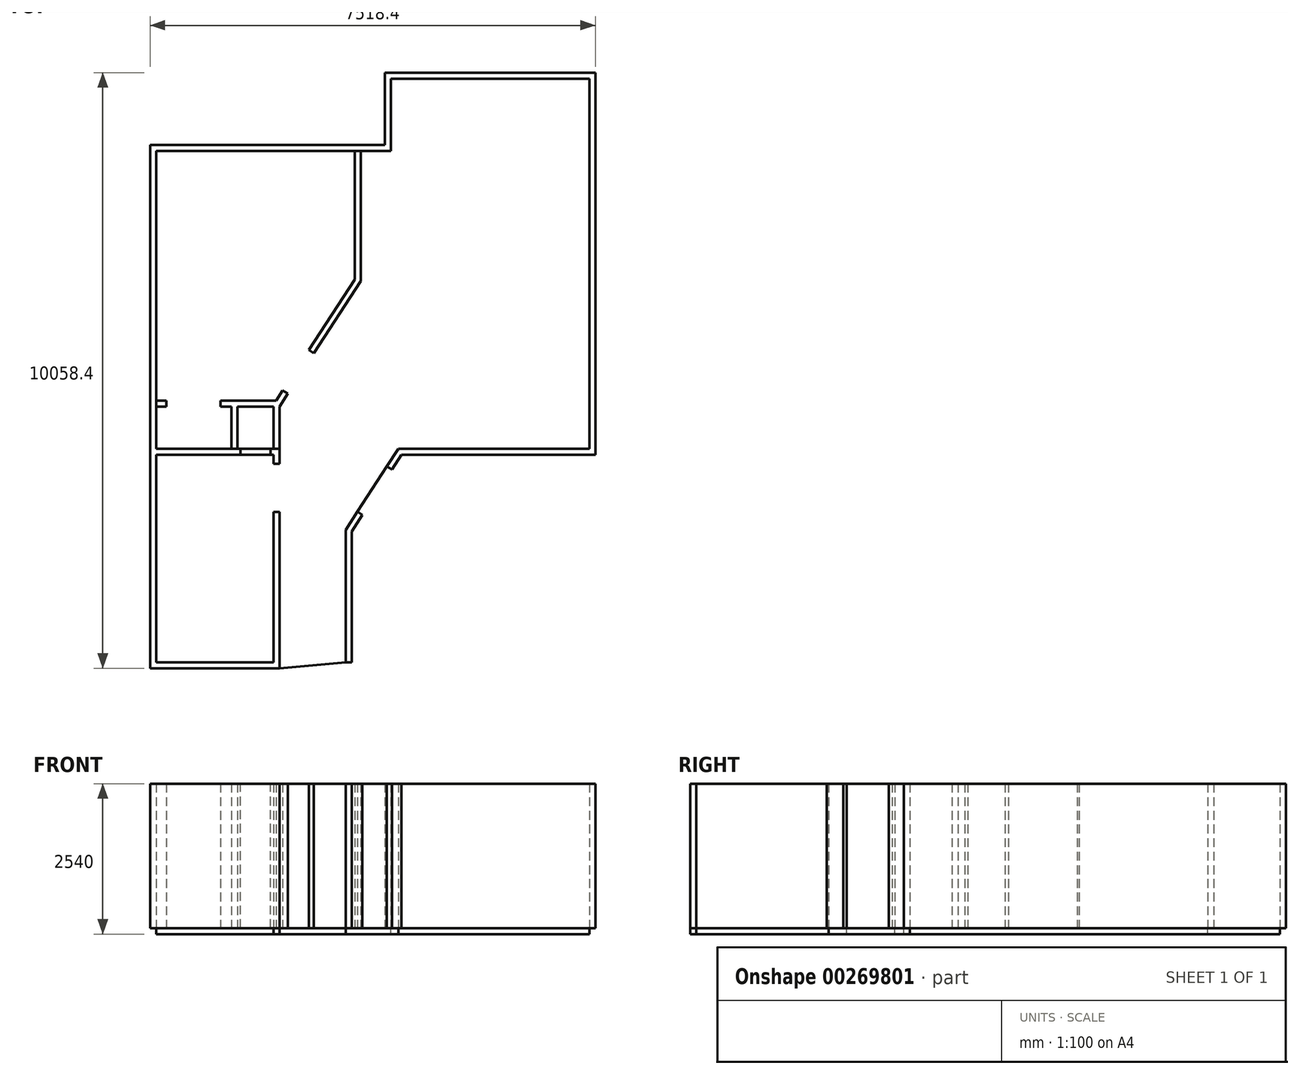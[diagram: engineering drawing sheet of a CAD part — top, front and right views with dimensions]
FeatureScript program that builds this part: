
annotation { "Feature Type Name" : "Feature", "Feature Type Description" : "" }
export const myFeature = defineFeature(function(context is Context, id is Id, definition is map)
    precondition{}
    {
        {
            var Q0;
            Q0=qCreatedBy(makeId("Top.planeOp"),FACE);
            var sketch = newSketch(context, id + "F0", { "sketchPlane" : qUnion([Q0])});
            skLineSegment(sketch, "E0", {"start": v(-1219.2, -1524) * mm, "end": v(-1219.2, -3606.8) * mm});
            skLineSegment(sketch, "E1", {"start": v(-1219.2, -3606.8) * mm, "end": v(-3200.4, -3606.8) * mm});
            skLineSegment(sketch, "E2", {"start": v(-3200.4, -3606.8) * mm, "end": v(-3200.4, -101.6) * mm});
            skLineSegment(sketch, "E3", {"start": v(-3200.4, 5029.2) * mm, "end": v(762, 5029.2) * mm});
            skLineSegment(sketch, "E4", {"start": v(762, 5029.2) * mm, "end": v(762, 6248.4) * mm});
            skLineSegment(sketch, "E5", {"start": v(762, 6248.4) * mm, "end": v(4114.8, 6248.4) * mm});
            skLineSegment(sketch, "E6", {"start": v(4114.8, 6248.4) * mm, "end": v(4114.8, 0) * mm});
            skLineSegment(sketch, "E7", {"start": v(4114.8, 0) * mm, "end": v(889, 0) * mm});
            skLineSegment(sketch, "E8", {"start": v(889, 0) * mm, "end": v(695.46, -298.6) * mm});
            skLineSegment(sketch, "E9", {"start": v(0, -1371.6) * mm, "end": v(0, -3606.8) * mm});
            skLineSegment(sketch, "E10", {"start": v(-1117.6, -1524) * mm, "end": v(-1117.6, -3606.8) * mm});
            skLineSegment(sketch, "E11.0", {"start": v(101.6, -1401.65) * mm, "end": v(101.6, -3606.8) * mm});
            skLineSegment(sketch, "E11.1", {"start": v(944.22, -101.6) * mm, "end": v(780.72, -353.87) * mm});
            skLineSegment(sketch, "E11.2", {"start": v(4216.4, -101.6) * mm, "end": v(944.22, -101.6) * mm});
            skLineSegment(sketch, "E11.3", {"start": v(4216.4, 6350) * mm, "end": v(4216.4, -101.6) * mm});
            skLineSegment(sketch, "E11.4", {"start": v(660.4, 6350) * mm, "end": v(4216.4, 6350) * mm});
            skLineSegment(sketch, "E11.5", {"start": v(-1648.96, -3708.4) * mm, "end": v(-3302, -3708.4) * mm});
            skLineSegment(sketch, "E11.6", {"start": v(-3302, -3708.4) * mm, "end": v(-3302, 5130.8) * mm});
            skLineSegment(sketch, "E11.7", {"start": v(-3302, 5130.8) * mm, "end": v(660.4, 5130.8) * mm});
            skLineSegment(sketch, "E11.8", {"start": v(660.4, 5130.8) * mm, "end": v(660.4, 6350) * mm});
            skLineSegment(sketch, "E12", {"start": v(-1117.6, -3606.8) * mm, "end": v(-1117.6, -3708.4) * mm});
            skLineSegment(sketch, "E13", {"start": v(-1117.6, -3708.4) * mm, "end": v(-1648.96, -3708.4) * mm});
            skLineSegment(sketch, "E14", {"start": v(0, -3606.8) * mm, "end": v(101.6, -3606.8) * mm});
            skLineSegment(sketch, "E15", {"start": v(-1219.2, -1524) * mm, "end": v(-1219.2, -1066.8) * mm});
            skLineSegment(sketch, "E16", {"start": v(-1219.2, -101.6) * mm, "end": v(-3200.4, -101.6) * mm});
            skLineSegment(sketch, "E17", {"start": v(-3200.4, 0) * mm, "end": v(-1117.6, 0) * mm});
            skLineSegment(sketch, "E18", {"start": v(-1117.6, 0) * mm, "end": v(-1117.6, -254) * mm});
            skLineSegment(sketch, "E19.trimOffspring", {"start": v(-3200.4, 0) * mm, "end": v(-3200.4, 5029.2) * mm});
            skLineSegment(sketch, "E20", {"start": v(-1219.2, -254) * mm, "end": v(-1117.6, -254) * mm});
            skLineSegment(sketch, "E21", {"start": v(-1219.2, -1066.8) * mm, "end": v(-1117.6, -1066.8) * mm});
            skLineSegment(sketch, "E22.trimOffspring", {"start": v(-1219.2, -254) * mm, "end": v(-1219.2, -101.6) * mm});
            skLineSegment(sketch, "E23.trimOffspring", {"start": v(-1117.6, -1066.8) * mm, "end": v(-1117.6, -1524) * mm});
            skLineSegment(sketch, "E24", {"start": v(198.12, -1065.93) * mm, "end": v(283.38, -1121.19) * mm});
            skLineSegment(sketch, "E25", {"start": v(695.46, -298.6) * mm, "end": v(780.72, -353.87) * mm});
            skLineSegment(sketch, "E26.trimOffspring", {"start": v(198.12, -1065.93) * mm, "end": v(0, -1371.6) * mm});
            skLineSegment(sketch, "E27.trimOffspring", {"start": v(283.38, -1121.19) * mm, "end": v(101.6, -1401.65) * mm});
            skSolve(sketch);
        }
        {
            var Q0;
            Q0=makeQuery(id+"F0.imprint","IMPRINT",FACE,{"disambiguationData":[TD([[makeQuery(id+"F0.imprint","IMPRINT",EDGE,{"derivedFrom":sQuery(id+"F0.wireOp",EDGE,"E0")}),1.0]])]});
            var Q1;
            Q1=makeQuery(id+"F0.imprint","IMPRINT",FACE,{"disambiguationData":[TD([[makeQuery(id+"F0.imprint","IMPRINT",EDGE,{"derivedFrom":sQuery(id+"F0.wireOp",EDGE,"E9")}),1.0]])]});
            extrude(context, id + "F1", {"entities" : qUnion([Q0, Q1]), "depth" : 2438.4 * mm});
        }
        {
            var Q0;
            Q0=qCreatedBy(makeId("Top.planeOp"),FACE);
            var sketch = newSketch(context, id + "F2", { "sketchPlane" : qUnion([Q0])});
            skLineSegment(sketch, "E28.0", {"start": v(-3200.4, 5029.2) * mm, "end": v(762, 5029.2) * mm});
            skLineSegment(sketch, "E29.0", {"start": v(-3200.4, 0) * mm, "end": v(-3200.4, 5029.2) * mm});
            skLineSegment(sketch, "E30.0", {"start": v(-3200.4, 0) * mm, "end": v(-1117.6, 0) * mm});
            skPoint(sketch, "E31.0", {"position": v(-1117.6, -127) * mm});
            skLineSegment(sketch, "E32.0", {"start": v(-1117.6, 0) * mm, "end": v(-1117.6, -254) * mm});
            skLineSegment(sketch, "E33.0", {"start": v(-1219.2, -254) * mm, "end": v(-1117.6, -254) * mm});
            skLineSegment(sketch, "E34.0", {"start": v(-1219.2, -254) * mm, "end": v(-1219.2, -101.6) * mm});
            skLineSegment(sketch, "E35.0", {"start": v(-1219.2, -101.6) * mm, "end": v(-3200.4, -101.6) * mm});
            skLineSegment(sketch, "E36.0", {"start": v(-3200.4, -3606.8) * mm, "end": v(-3200.4, -101.6) * mm});
            skLineSegment(sketch, "E37.0", {"start": v(-1219.2, -3606.8) * mm, "end": v(-3200.4, -3606.8) * mm});
            skLineSegment(sketch, "E38.0", {"start": v(-1219.2, -3606.8) * mm, "end": v(-1219.2, -1066.8) * mm});
            skLineSegment(sketch, "E39.0", {"start": v(-1219.2, -1066.8) * mm, "end": v(-1117.6, -1066.8) * mm});
            skLineSegment(sketch, "E40.0", {"start": v(-1117.6, -1066.8) * mm, "end": v(-1117.6, -3708.4) * mm});
            skLineSegment(sketch, "E41.0", {"start": v(0, -1371.6) * mm, "end": v(0, -3606.8) * mm});
            skLineSegment(sketch, "E42.0", {"start": v(198.12, -1065.93) * mm, "end": v(0, -1371.6) * mm});
            skLineSegment(sketch, "E43.0", {"start": v(4114.8, 0) * mm, "end": v(889, 0) * mm});
            skLineSegment(sketch, "E44.0", {"start": v(4114.8, 6248.4) * mm, "end": v(4114.8, 0) * mm});
            skLineSegment(sketch, "E45.0", {"start": v(762, 6248.4) * mm, "end": v(4114.8, 6248.4) * mm});
            skLineSegment(sketch, "E46.0", {"start": v(762, 5029.2) * mm, "end": v(762, 6248.4) * mm});
            skLineSegment(sketch, "E47", {"start": v(-1117.6, -3708.4) * mm, "end": v(0, -3606.8) * mm});
            skLineSegment(sketch, "E48", {"start": v(889, 0) * mm, "end": v(198.12, -1065.93) * mm});
            skSolve(sketch);
        }
        {
            var Q0;
            Q0=makeQuery(id+"F2.imprint","IMPRINT",FACE,{"disambiguationData":[TD([[makeQuery(id+"F2.imprint","IMPRINT",EDGE,{"derivedFrom":sQuery(id+"F2.wireOp",EDGE,"E28.0")}),-1.0]])]});
            extrude(context, id + "F3", {"entities" : qUnion([Q0]), "oppositeDirection" : true, "depth" : 101.6 * mm});
        }
        {
            var Q0;
            Q0=qCreatedBy(makeId("Top.planeOp"),FACE);
            var sketch = newSketch(context, id + "F4", { "sketchPlane" : qUnion([Q0])});
            skLineSegment(sketch, "E49", {"start": v(152.4, 5029.2) * mm, "end": v(152.4, 2857.43) * mm});
            skLineSegment(sketch, "E50", {"start": v(152.4, 2857.43) * mm, "end": v(-620.22, 1665.38) * mm});
            skLineSegment(sketch, "E51", {"start": v(-1172.82, 812.8) * mm, "end": v(-2111.35, 812.8) * mm});
            skLineSegment(sketch, "E52.0", {"start": v(152.4, 5029.2) * mm, "end": v(254, 5029.2) * mm});
            skLineSegment(sketch, "E53", {"start": v(254, 5029.2) * mm, "end": v(254, 2827.38) * mm});
            skLineSegment(sketch, "E54", {"start": v(254, 2827.38) * mm, "end": v(-534.97, 1610.12) * mm});
            skLineSegment(sketch, "E55", {"start": v(-1219.2, 711.2) * mm, "end": v(-1828.8, 711.2) * mm});
            skLineSegment(sketch, "E56", {"start": v(-3200.4, 812.8) * mm, "end": v(-3200.4, 711.2) * mm});
            skPoint(sketch, "E57.orphan", {"position": v(-3200.4, 5029.2) * mm});
            skPoint(sketch, "E58.orphan", {"position": v(762, 5029.2) * mm});
            skLineSegment(sketch, "E59", {"start": v(-1117.6, 711.2) * mm, "end": v(-1117.6, 0) * mm});
            skLineSegment(sketch, "E60", {"start": v(-1219.2, 711.2) * mm, "end": v(-1219.2, 0) * mm});
            skLineSegment(sketch, "E61", {"start": v(-1219.2, 0) * mm, "end": v(-1117.6, 0) * mm});
            skLineSegment(sketch, "E62", {"start": v(-1828.8, 711.2) * mm, "end": v(-1828.8, 0) * mm});
            skLineSegment(sketch, "E63", {"start": v(-1930.4, 711.2) * mm, "end": v(-1930.4, 0) * mm});
            skLineSegment(sketch, "E64.trimOffspring", {"start": v(-1930.4, 711.2) * mm, "end": v(-2111.35, 711.2) * mm});
            skLineSegment(sketch, "E65", {"start": v(-1930.4, 0) * mm, "end": v(-1828.8, 0) * mm});
            skLineSegment(sketch, "E66", {"start": v(-3025.75, 812.8) * mm, "end": v(-3025.75, 711.2) * mm});
            skLineSegment(sketch, "E67", {"start": v(-2111.35, 812.8) * mm, "end": v(-2111.35, 711.2) * mm});
            skLineSegment(sketch, "E68.trimOffspring", {"start": v(-3025.75, 812.8) * mm, "end": v(-3200.4, 812.8) * mm});
            skLineSegment(sketch, "E69.trimOffspring", {"start": v(-3025.75, 711.2) * mm, "end": v(-3200.4, 711.2) * mm});
            skLineSegment(sketch, "E70.bottom", {"start": v(-3194.1, 4486.37) * mm, "end": v(-1162.1, 4486.37) * mm, "construction": true});
            skLineSegment(sketch, "E70.top", {"start": v(-3194.1, 2962.37) * mm, "end": v(-1162.1, 2962.37) * mm, "construction": true});
            skLineSegment(sketch, "E70.left", {"start": v(-3194.1, 4486.37) * mm, "end": v(-3194.1, 2962.37) * mm, "construction": true});
            skLineSegment(sketch, "E70.right", {"start": v(-1162.1, 4486.37) * mm, "end": v(-1162.1, 2962.37) * mm, "construction": true});
            skLineSegment(sketch, "E71", {"start": v(-1062.3, 983.32) * mm, "end": v(-977.05, 928.06) * mm});
            skLineSegment(sketch, "E72", {"start": v(-620.22, 1665.38) * mm, "end": v(-534.97, 1610.12) * mm});
            skLineSegment(sketch, "E73.trimOffspring", {"start": v(-1062.3, 983.32) * mm, "end": v(-1172.82, 812.8) * mm});
            skLineSegment(sketch, "E74.trimOffspring", {"start": v(-977.05, 928.06) * mm, "end": v(-1117.6, 711.2) * mm});
            skSolve(sketch);
        }
        {
            var Q0;
            Q0=makeQuery(id+"F4.imprint","IMPRINT",FACE,{"disambiguationData":[TD([[makeQuery(id+"F4.imprint","IMPRINT",EDGE,{"derivedFrom":sQuery(id+"F4.wireOp",EDGE,"E49")}),1.0]])]});
            var Q1;
            Q1=makeQuery(id+"F4.imprint","IMPRINT",FACE,{"disambiguationData":[TD([[makeQuery(id+"F4.imprint","IMPRINT",EDGE,{"derivedFrom":sQuery(id+"F4.wireOp",EDGE,"E51")}),1.0]])]});
            var Q2;
            Q2=makeQuery(id+"F4.imprint","IMPRINT",FACE,{"disambiguationData":[TD([[makeQuery(id+"F4.imprint","IMPRINT",EDGE,{"derivedFrom":sQuery(id+"F4.wireOp",EDGE,"E56")}),1.0]])]});
            extrude(context, id + "F5", {"entities" : qUnion([Q0, Q1, Q2]), "depth" : 2438.4 * mm});
        }
        {
            var Q0;
            Q0=qCreatedBy(makeId("Top.planeOp"),FACE);
            var sketch = newSketch(context, id + "F6", { "sketchPlane" : qUnion([Q0])});
            skLineSegment(sketch, "E75.bottom", {"start": v(-1778, 162.07) * mm, "end": v(-1270, 162.07) * mm});
            skLineSegment(sketch, "E75.top", {"start": v(-1778, -226.65) * mm, "end": v(-1270, -226.65) * mm});
            skLineSegment(sketch, "E75.left", {"start": v(-1778, 162.07) * mm, "end": v(-1778, -226.65) * mm});
            skLineSegment(sketch, "E75.right", {"start": v(-1270, 162.07) * mm, "end": v(-1270, -226.65) * mm});
            skSolve(sketch);
        }
        {
            var Q0;
            Q0=makeQuery(id+"F6.imprint","IMPRINT",FACE,{"disambiguationData":[TD([[makeQuery(id+"F6.imprint","IMPRINT",EDGE,{"derivedFrom":sQuery(id+"F6.wireOp",EDGE,"E75.bottom")}),-1.0]])]});
            var Q1;
            Q1=makeQuery(id+"F1.opExtrude","CAP_FACE",FACE,{"disambiguationData":[OSD([sQuery(id+"F0.wireOp",EDGE,"E0"),sQuery(id+"F0.wireOp",EDGE,"E1"),sQuery(id+"F0.wireOp",EDGE,"E2"),sQuery(id+"F0.wireOp",EDGE,"E3"),sQuery(id+"F0.wireOp",EDGE,"E4"),sQuery(id+"F0.wireOp",EDGE,"E5"),sQuery(id+"F0.wireOp",EDGE,"E6"),sQuery(id+"F0.wireOp",EDGE,"E7"),sQuery(id+"F0.wireOp",EDGE,"E8"),sQuery(id+"F0.wireOp",EDGE,"E10"),sQuery(id+"F0.wireOp",EDGE,"E11.1"),sQuery(id+"F0.wireOp",EDGE,"E11.2"),sQuery(id+"F0.wireOp",EDGE,"E11.3"),sQuery(id+"F0.wireOp",EDGE,"E11.4"),sQuery(id+"F0.wireOp",EDGE,"E11.5"),sQuery(id+"F0.wireOp",EDGE,"E11.6"),sQuery(id+"F0.wireOp",EDGE,"E11.7"),sQuery(id+"F0.wireOp",EDGE,"E11.8"),sQuery(id+"F0.wireOp",EDGE,"E12"),sQuery(id+"F0.wireOp",EDGE,"E13"),sQuery(id+"F0.wireOp",EDGE,"E15"),sQuery(id+"F0.wireOp",EDGE,"E16"),sQuery(id+"F0.wireOp",EDGE,"E17"),sQuery(id+"F0.wireOp",EDGE,"E18"),sQuery(id+"F0.wireOp",EDGE,"E19.trimOffspring"),sQuery(id+"F0.wireOp",EDGE,"E20"),sQuery(id+"F0.wireOp",EDGE,"E21"),sQuery(id+"F0.wireOp",EDGE,"E22.trimOffspring"),sQuery(id+"F0.wireOp",EDGE,"E23.trimOffspring"),sQuery(id+"F0.wireOp",EDGE,"E25")])],"isStart":false});
            extrude(context, id + "F7", {"entities" : qUnion([Q0]), "endBound" : BoundingType.UP_TO_SURFACE, "endBoundEntityFace" : qUnion([Q1]), "depth" : 25.4 * mm});
        }
        {
            var Q0;
            Q0=makeQuery(id+"F7.opExtrude","SWEPT_BODY",BODY,{"disambiguationData":[OSD([sQuery(id+"F6.wireOp",EDGE,"E75.bottom"),sQuery(id+"F6.wireOp",EDGE,"E75.top"),sQuery(id+"F6.wireOp",EDGE,"E75.left"),sQuery(id+"F6.wireOp",EDGE,"E75.right")])]});
            var Q1;
            Q1=makeQuery(id+"F1.opExtrude","SWEPT_BODY",BODY,{"disambiguationData":[OSD([sQuery(id+"F0.wireOp",EDGE,"E0"),sQuery(id+"F0.wireOp",EDGE,"E1"),sQuery(id+"F0.wireOp",EDGE,"E2"),sQuery(id+"F0.wireOp",EDGE,"E3"),sQuery(id+"F0.wireOp",EDGE,"E4"),sQuery(id+"F0.wireOp",EDGE,"E5"),sQuery(id+"F0.wireOp",EDGE,"E6"),sQuery(id+"F0.wireOp",EDGE,"E7"),sQuery(id+"F0.wireOp",EDGE,"E8"),sQuery(id+"F0.wireOp",EDGE,"E10"),sQuery(id+"F0.wireOp",EDGE,"E11.1"),sQuery(id+"F0.wireOp",EDGE,"E11.2"),sQuery(id+"F0.wireOp",EDGE,"E11.3"),sQuery(id+"F0.wireOp",EDGE,"E11.4"),sQuery(id+"F0.wireOp",EDGE,"E11.5"),sQuery(id+"F0.wireOp",EDGE,"E11.6"),sQuery(id+"F0.wireOp",EDGE,"E11.7"),sQuery(id+"F0.wireOp",EDGE,"E11.8"),sQuery(id+"F0.wireOp",EDGE,"E12"),sQuery(id+"F0.wireOp",EDGE,"E13"),sQuery(id+"F0.wireOp",EDGE,"E15"),sQuery(id+"F0.wireOp",EDGE,"E16"),sQuery(id+"F0.wireOp",EDGE,"E17"),sQuery(id+"F0.wireOp",EDGE,"E18"),sQuery(id+"F0.wireOp",EDGE,"E19.trimOffspring"),sQuery(id+"F0.wireOp",EDGE,"E20"),sQuery(id+"F0.wireOp",EDGE,"E21"),sQuery(id+"F0.wireOp",EDGE,"E22.trimOffspring"),sQuery(id+"F0.wireOp",EDGE,"E23.trimOffspring"),sQuery(id+"F0.wireOp",EDGE,"E25")])]});
            booleanBodies(context, id + "F8", {"operationType" : BooleanOperationType.SUBTRACTION, "tools" : qUnion([Q0]), "targets" : qUnion([Q1])});
        }
    });
